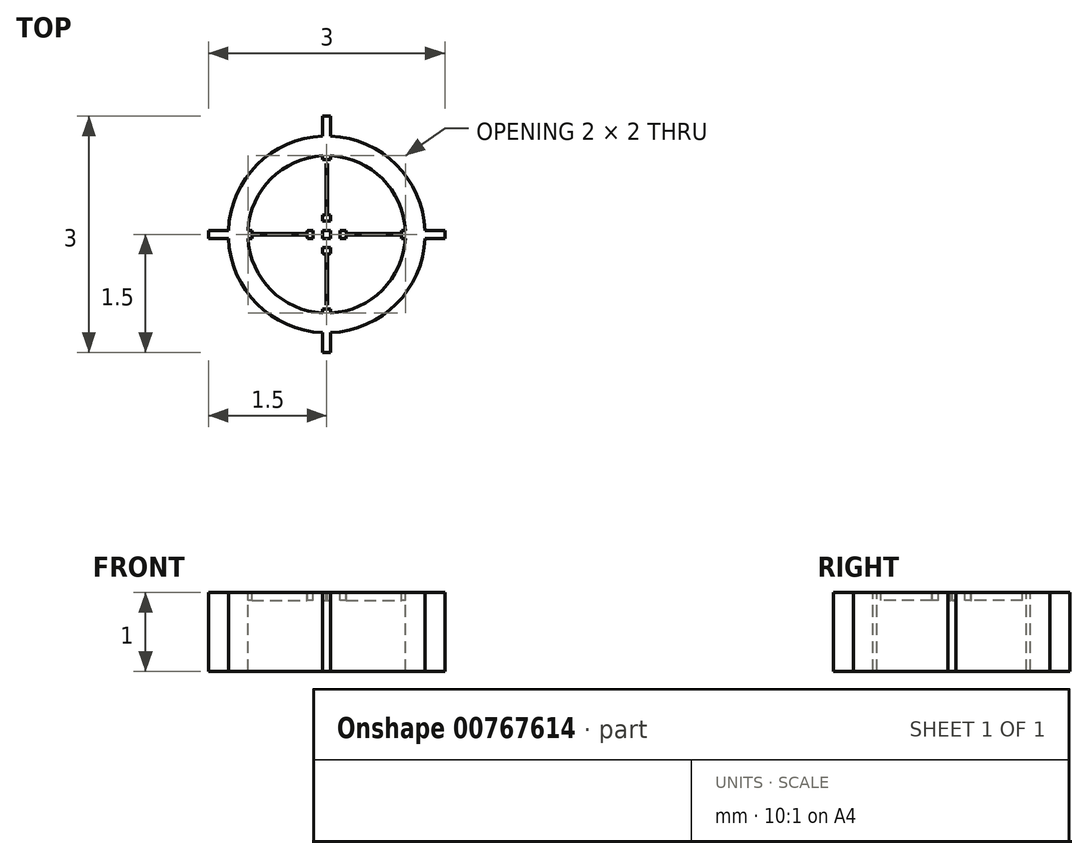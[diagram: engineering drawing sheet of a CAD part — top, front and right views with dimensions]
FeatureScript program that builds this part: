
annotation { "Feature Type Name" : "Feature", "Feature Type Description" : "" }
export const myFeature = defineFeature(function(context is Context, id is Id, definition is map)
    precondition{}
    {
        {
            var Q0;
            Q0=qCreatedBy(makeId("Top.planeOp"),FACE);
            var sketch = newSketch(context, id + "F0", { "sketchPlane" : qUnion([Q0])});
            skCircle(sketch, "E0", {"center": v(0, 0) * mm, "radius": 1 * mm});
            skCircle(sketch, "E1", {"center": v(0, 0) * mm, "radius": 1.25 * mm});
            skLineSegment(sketch, "E2.bottom", {"start": v(1.5, 0.05) * mm, "end": v(-1.5, 0.05) * mm});
            skLineSegment(sketch, "E2.top", {"start": v(1.5, -0.05) * mm, "end": v(-1.5, -0.05) * mm});
            skLineSegment(sketch, "E2.left", {"start": v(1.5, 0.05) * mm, "end": v(1.5, -0.05) * mm});
            skLineSegment(sketch, "E2.right", {"start": v(-1.5, 0.05) * mm, "end": v(-1.5, -0.05) * mm});
            skLineSegment(sketch, "E3.bottom", {"start": v(0.05, 1.5) * mm, "end": v(-0.05, 1.5) * mm});
            skLineSegment(sketch, "E3.top", {"start": v(0.05, -1.5) * mm, "end": v(-0.05, -1.5) * mm});
            skLineSegment(sketch, "E3.left", {"start": v(0.05, 1.5) * mm, "end": v(0.05, -1.5) * mm});
            skLineSegment(sketch, "E3.right", {"start": v(-0.05, 1.5) * mm, "end": v(-0.05, -1.5) * mm});
            skCircle(sketch, "E4", {"center": v(0, 0) * mm, "radius": 0.04 * mm});
            skLineSegment(sketch, "E5.bottom", {"start": v(-0.95, 0.05) * mm, "end": v(-0.17, 0.05) * mm});
            skLineSegment(sketch, "E5.top", {"start": v(-0.95, -0.05) * mm, "end": v(-0.17, -0.05) * mm});
            skLineSegment(sketch, "E5.left", {"start": v(-0.95, 0.05) * mm, "end": v(-0.95, -0.05) * mm});
            skLineSegment(sketch, "E5.right", {"start": v(-0.17, 0.05) * mm, "end": v(-0.17, -0.05) * mm});
            skLineSegment(sketch, "E6.bottom", {"start": v(-0.95, 0) * mm, "end": v(-0.17, 0) * mm});
            skLineSegment(sketch, "E6.top", {"start": v(-0.95, -0.01) * mm, "end": v(-0.17, -0.01) * mm});
            skLineSegment(sketch, "E6.left", {"start": v(-0.95, 0) * mm, "end": v(-0.95, -0.01) * mm});
            skLineSegment(sketch, "E6.right", {"start": v(-0.17, 0) * mm, "end": v(-0.17, -0.01) * mm});
            skLineSegment(sketch, "E7.bottom", {"start": v(0.17, 0.05) * mm, "end": v(0.95, 0.05) * mm});
            skLineSegment(sketch, "E7.top", {"start": v(0.17, -0.05) * mm, "end": v(0.95, -0.05) * mm});
            skLineSegment(sketch, "E7.left", {"start": v(0.17, 0.05) * mm, "end": v(0.17, -0.05) * mm});
            skLineSegment(sketch, "E7.right", {"start": v(0.95, 0.05) * mm, "end": v(0.95, -0.05) * mm});
            skLineSegment(sketch, "E8.bottom", {"start": v(0.17, 0) * mm, "end": v(0.95, 0) * mm});
            skLineSegment(sketch, "E8.top", {"start": v(0.17, -0.01) * mm, "end": v(0.95, -0.01) * mm});
            skLineSegment(sketch, "E8.left", {"start": v(0.17, 0) * mm, "end": v(0.17, -0.01) * mm});
            skLineSegment(sketch, "E8.right", {"start": v(0.95, 0) * mm, "end": v(0.95, -0.01) * mm});
            skLineSegment(sketch, "E9.bottom", {"start": v(-0.05, 0.95) * mm, "end": v(0.05, 0.95) * mm});
            skLineSegment(sketch, "E9.top", {"start": v(-0.05, 0.17) * mm, "end": v(0.05, 0.17) * mm});
            skLineSegment(sketch, "E9.left", {"start": v(-0.05, 0.95) * mm, "end": v(-0.05, 0.17) * mm});
            skLineSegment(sketch, "E9.right", {"start": v(0.05, 0.95) * mm, "end": v(0.05, 0.17) * mm});
            skLineSegment(sketch, "E10.bottom", {"start": v(0, 0.95) * mm, "end": v(0.01, 0.95) * mm});
            skLineSegment(sketch, "E10.top", {"start": v(0, 0.17) * mm, "end": v(0.01, 0.17) * mm});
            skLineSegment(sketch, "E10.left", {"start": v(0, 0.95) * mm, "end": v(0, 0.17) * mm});
            skLineSegment(sketch, "E10.right", {"start": v(0.01, 0.95) * mm, "end": v(0.01, 0.17) * mm});
            skLineSegment(sketch, "E11.bottom", {"start": v(-0.05, -0.95) * mm, "end": v(0.05, -0.95) * mm});
            skLineSegment(sketch, "E11.top", {"start": v(-0.05, -0.17) * mm, "end": v(0.05, -0.17) * mm});
            skLineSegment(sketch, "E11.left", {"start": v(-0.05, -0.95) * mm, "end": v(-0.05, -0.17) * mm});
            skLineSegment(sketch, "E11.right", {"start": v(0.05, -0.95) * mm, "end": v(0.05, -0.17) * mm});
            skLineSegment(sketch, "E12.bottom", {"start": v(0, -0.17) * mm, "end": v(0.01, -0.17) * mm});
            skLineSegment(sketch, "E12.top", {"start": v(0, -0.95) * mm, "end": v(0.01, -0.95) * mm});
            skLineSegment(sketch, "E12.left", {"start": v(0, -0.17) * mm, "end": v(0, -0.95) * mm});
            skLineSegment(sketch, "E12.right", {"start": v(0.01, -0.17) * mm, "end": v(0.01, -0.95) * mm});
            skCircle(sketch, "E13", {"center": v(0, 0) * mm, "radius": 0.9 * mm});
            skCircle(sketch, "E14", {"center": v(0, 0) * mm, "radius": 0.25 * mm});
            skSolve(sketch);
        }
        {
            var Q0;
            Q0=makeQuery(id+"F0.imprint","IMPRINT",FACE,{"disambiguationData":[TD([[makeQuery(id+"F0.imprint","IMPRINT",EDGE,{"derivedFrom":sQuery(id+"F0.wireOp",EDGE,"E0")}),-1.0]])]});
            var Q1;
            {var subQ3=sQuery(id+"F0.wireOp",EDGE,"E6.left");Q1=makeQuery(id+"F0.imprint","IMPRINT",FACE,{"disambiguationData":[TD([[makeQuery(id+"F0.imprint","IMPRINT",EDGE,{"derivedFrom":subQ3}),-1.0]])]});}
            var Q2;
            {var subQ0=sQuery(id+"F0.wireOp",EDGE,"E3.left");var subQ1=sQuery(id+"F0.wireOp",EDGE,"E0");var subQ2=makeQuery(id+"F0.imprint","INTERSECT",VERTEX,{"disambiguationData":[OD(0.0)],"derivedFrom":[subQ1,subQ0]});Q2=makeQuery(id+"F0.imprint","IMPRINT",FACE,{"disambiguationData":[TD([[makeQuery(id+"F0.imprint","IMPRINT",EDGE,{"disambiguationData":[TD([[subQ2,-1.0]])],"derivedFrom":subQ1}),1.0]])]});}
            var Q3;
            {var subQ0=sQuery(id+"F0.wireOp",EDGE,"E3.right");var subQ1=sQuery(id+"F0.wireOp",EDGE,"E0");var subQ2=makeQuery(id+"F0.imprint","INTERSECT",VERTEX,{"disambiguationData":[OD(1.0)],"derivedFrom":[subQ1,subQ0]});Q3=makeQuery(id+"F0.imprint","IMPRINT",FACE,{"disambiguationData":[TD([[makeQuery(id+"F0.imprint","IMPRINT",EDGE,{"disambiguationData":[TD([[subQ2,-1.0]])],"derivedFrom":subQ1}),1.0]])]});}
            var Q4;
            {var subQ7=sQuery(id+"F0.wireOp",EDGE,"E8.right");Q4=makeQuery(id+"F0.imprint","IMPRINT",FACE,{"disambiguationData":[TD([[makeQuery(id+"F0.imprint","IMPRINT",EDGE,{"derivedFrom":subQ7}),1.0]])]});}
            var Q5;
            {var subQ5=sQuery(id+"F0.wireOp",EDGE,"E2.right");Q5=makeQuery(id+"F0.imprint","IMPRINT",FACE,{"disambiguationData":[TD([[makeQuery(id+"F0.imprint","IMPRINT",EDGE,{"derivedFrom":subQ5}),1.0]])]});}
            var Q6;
            {var subQ5=sQuery(id+"F0.wireOp",EDGE,"E3.bottom");Q6=makeQuery(id+"F0.imprint","IMPRINT",FACE,{"disambiguationData":[TD([[makeQuery(id+"F0.imprint","IMPRINT",EDGE,{"derivedFrom":subQ5}),1.0]])]});}
            var Q7;
            {var subQ5=sQuery(id+"F0.wireOp",EDGE,"E2.left");Q7=makeQuery(id+"F0.imprint","IMPRINT",FACE,{"disambiguationData":[TD([[makeQuery(id+"F0.imprint","IMPRINT",EDGE,{"derivedFrom":subQ5}),-1.0]])]});}
            var Q8;
            {var subQ5=sQuery(id+"F0.wireOp",EDGE,"E3.top");Q8=makeQuery(id+"F0.imprint","IMPRINT",FACE,{"disambiguationData":[TD([[makeQuery(id+"F0.imprint","IMPRINT",EDGE,{"derivedFrom":subQ5}),-1.0]])]});}
            extrude(context, id + "F1", {"entities" : qUnion([Q0, Q1, Q2, Q3, Q4, Q5, Q6, Q7, Q8]), "oppositeDirection" : true, "depth" : 1 * mm, "offsetDistance" : 25 * mm});
        }
        {
            var Q0;
            {var subQ5=sQuery(id+"F0.wireOp",EDGE,"E2.right");Q0=makeQuery(id+"F0.imprint","IMPRINT",FACE,{"disambiguationData":[TD([[makeQuery(id+"F0.imprint","IMPRINT",EDGE,{"derivedFrom":subQ5}),1.0]])]});}
            var Q1;
            {var subQ0=sQuery(id+"F0.wireOp",EDGE,"E2.bottom");var subQ1=sQuery(id+"F0.wireOp",EDGE,"E0");var subQ2=makeQuery(id+"F0.imprint","INTERSECT",VERTEX,{"disambiguationData":[OD(1.0)],"derivedFrom":[subQ1,subQ0]});Q1=makeQuery(id+"F0.imprint","IMPRINT",FACE,{"disambiguationData":[TD([[makeQuery(id+"F0.imprint","IMPRINT",EDGE,{"disambiguationData":[TD([[subQ2,-1.0]])],"derivedFrom":subQ1}),-1.0]])]});}
            var Q2;
            {var subQ0=sQuery(id+"F0.wireOp",EDGE,"E2.bottom");var subQ1=sQuery(id+"F0.wireOp",EDGE,"E0");var subQ2=makeQuery(id+"F0.imprint","INTERSECT",VERTEX,{"disambiguationData":[OD(1.0)],"derivedFrom":[subQ1,subQ0]});Q2=makeQuery(id+"F0.imprint","IMPRINT",FACE,{"disambiguationData":[TD([[makeQuery(id+"F0.imprint","IMPRINT",EDGE,{"disambiguationData":[TD([[subQ2,-1.0]])],"derivedFrom":subQ1}),1.0]])]});}
            var Q3;
            {var subQ0=sQuery(id+"F0.wireOp",EDGE,"E2.bottom");var subQ1=sQuery(id+"F0.wireOp",EDGE,"E0");var subQ2=makeQuery(id+"F0.imprint","INTERSECT",VERTEX,{"disambiguationData":[OD(0.0)],"derivedFrom":[subQ1,subQ0]});Q3=makeQuery(id+"F0.imprint","IMPRINT",FACE,{"disambiguationData":[TD([[makeQuery(id+"F0.imprint","IMPRINT",EDGE,{"disambiguationData":[TD([[subQ2,1.0]])],"derivedFrom":subQ1}),1.0]])]});}
            var Q4;
            {var subQ0=sQuery(id+"F0.wireOp",EDGE,"E2.bottom");var subQ1=sQuery(id+"F0.wireOp",EDGE,"E0");var subQ2=makeQuery(id+"F0.imprint","INTERSECT",VERTEX,{"disambiguationData":[OD(0.0)],"derivedFrom":[subQ1,subQ0]});Q4=makeQuery(id+"F0.imprint","IMPRINT",FACE,{"disambiguationData":[TD([[makeQuery(id+"F0.imprint","IMPRINT",EDGE,{"disambiguationData":[TD([[subQ2,1.0]])],"derivedFrom":subQ1}),-1.0]])]});}
            var Q5;
            {var subQ5=sQuery(id+"F0.wireOp",EDGE,"E2.left");Q5=makeQuery(id+"F0.imprint","IMPRINT",FACE,{"disambiguationData":[TD([[makeQuery(id+"F0.imprint","IMPRINT",EDGE,{"derivedFrom":subQ5}),-1.0]])]});}
            var Q6;
            {var subQ0=sQuery(id+"F0.wireOp",EDGE,"E3.left");var subQ1=sQuery(id+"F0.wireOp",EDGE,"E0");var subQ2=makeQuery(id+"F0.imprint","INTERSECT",VERTEX,{"disambiguationData":[OD(0.0)],"derivedFrom":[subQ1,subQ0]});Q6=makeQuery(id+"F0.imprint","IMPRINT",FACE,{"disambiguationData":[TD([[makeQuery(id+"F0.imprint","IMPRINT",EDGE,{"disambiguationData":[TD([[subQ2,-1.0]])],"derivedFrom":subQ1}),1.0]])]});}
            var Q7;
            {var subQ0=sQuery(id+"F0.wireOp",EDGE,"E3.left");var subQ1=sQuery(id+"F0.wireOp",EDGE,"E0");var subQ2=makeQuery(id+"F0.imprint","INTERSECT",VERTEX,{"disambiguationData":[OD(0.0)],"derivedFrom":[subQ1,subQ0]});Q7=makeQuery(id+"F0.imprint","IMPRINT",FACE,{"disambiguationData":[TD([[makeQuery(id+"F0.imprint","IMPRINT",EDGE,{"disambiguationData":[TD([[subQ2,-1.0]])],"derivedFrom":subQ1}),-1.0]])]});}
            var Q8;
            {var subQ5=sQuery(id+"F0.wireOp",EDGE,"E3.bottom");Q8=makeQuery(id+"F0.imprint","IMPRINT",FACE,{"disambiguationData":[TD([[makeQuery(id+"F0.imprint","IMPRINT",EDGE,{"derivedFrom":subQ5}),1.0]])]});}
            var Q9;
            {var subQ0=sQuery(id+"F0.wireOp",EDGE,"E3.right");var subQ1=sQuery(id+"F0.wireOp",EDGE,"E0");var subQ2=makeQuery(id+"F0.imprint","INTERSECT",VERTEX,{"disambiguationData":[OD(1.0)],"derivedFrom":[subQ1,subQ0]});Q9=makeQuery(id+"F0.imprint","IMPRINT",FACE,{"disambiguationData":[TD([[makeQuery(id+"F0.imprint","IMPRINT",EDGE,{"disambiguationData":[TD([[subQ2,-1.0]])],"derivedFrom":subQ1}),1.0]])]});}
            var Q10;
            {var subQ0=sQuery(id+"F0.wireOp",EDGE,"E3.right");var subQ1=sQuery(id+"F0.wireOp",EDGE,"E0");var subQ2=makeQuery(id+"F0.imprint","INTERSECT",VERTEX,{"disambiguationData":[OD(1.0)],"derivedFrom":[subQ1,subQ0]});Q10=makeQuery(id+"F0.imprint","IMPRINT",FACE,{"disambiguationData":[TD([[makeQuery(id+"F0.imprint","IMPRINT",EDGE,{"disambiguationData":[TD([[subQ2,-1.0]])],"derivedFrom":subQ1}),-1.0]])]});}
            var Q11;
            {var subQ5=sQuery(id+"F0.wireOp",EDGE,"E3.top");Q11=makeQuery(id+"F0.imprint","IMPRINT",FACE,{"disambiguationData":[TD([[makeQuery(id+"F0.imprint","IMPRINT",EDGE,{"derivedFrom":subQ5}),-1.0]])]});}
            var Q12;
            Q12=makeQuery(id+"F0.imprint","IMPRINT",FACE,{"disambiguationData":[TD([[makeQuery(id+"F0.imprint","IMPRINT",EDGE,{"derivedFrom":sQuery(id+"F0.wireOp",EDGE,"E4")}),1.0]])]});
            var Q13;
            Q13=makeQuery(id+"F0.imprint","IMPRINT",FACE,{"disambiguationData":[TD([[makeQuery(id+"F0.imprint","IMPRINT",EDGE,{"derivedFrom":sQuery(id+"F0.wireOp",EDGE,"E4")}),-1.0]])]});
            var Q14;
            Q14=makeQuery(id+"F0.imprint","IMPRINT",FACE,{"disambiguationData":[TD([[makeQuery(id+"F0.imprint","IMPRINT",EDGE,{"derivedFrom":sQuery(id+"F0.wireOp",EDGE,"E6.bottom")}),-1.0]])]});
            var Q15;
            {var subQ7=sQuery(id+"F0.wireOp",EDGE,"E6.right");Q15=makeQuery(id+"F0.imprint","IMPRINT",FACE,{"disambiguationData":[TD([[makeQuery(id+"F0.imprint","IMPRINT",EDGE,{"derivedFrom":subQ7}),1.0]])]});}
            var Q16;
            {var subQ5=sQuery(id+"F0.wireOp",EDGE,"E8.left");Q16=makeQuery(id+"F0.imprint","IMPRINT",FACE,{"disambiguationData":[TD([[makeQuery(id+"F0.imprint","IMPRINT",EDGE,{"derivedFrom":subQ5}),-1.0]])]});}
            var Q17;
            {var subQ8=sQuery(id+"F0.wireOp",EDGE,"E12.bottom");Q17=makeQuery(id+"F0.imprint","IMPRINT",FACE,{"disambiguationData":[TD([[makeQuery(id+"F0.imprint","IMPRINT",EDGE,{"derivedFrom":subQ8}),1.0]])]});}
            var Q18;
            Q18=makeQuery(id+"F0.imprint","IMPRINT",FACE,{"disambiguationData":[TD([[makeQuery(id+"F0.imprint","IMPRINT",EDGE,{"derivedFrom":sQuery(id+"F0.wireOp",EDGE,"E10.bottom")}),-1.0]])]});
            var Q19;
            Q19=makeQuery(id+"F0.imprint","IMPRINT",FACE,{"disambiguationData":[TD([[makeQuery(id+"F0.imprint","IMPRINT",EDGE,{"derivedFrom":sQuery(id+"F0.wireOp",EDGE,"E12.bottom")}),-1.0]])]});
            var Q20;
            Q20=makeQuery(id+"F0.imprint","IMPRINT",FACE,{"disambiguationData":[TD([[makeQuery(id+"F0.imprint","IMPRINT",EDGE,{"derivedFrom":sQuery(id+"F0.wireOp",EDGE,"E8.bottom")}),-1.0]])]});
            var Q21;
            {var subQ3=sQuery(id+"F0.wireOp",EDGE,"E10.top");Q21=makeQuery(id+"F0.imprint","IMPRINT",FACE,{"disambiguationData":[TD([[makeQuery(id+"F0.imprint","IMPRINT",EDGE,{"derivedFrom":subQ3}),-1.0]])]});}
            var Q22;
            {var subQ0=sQuery(id+"F0.wireOp",EDGE,"E10.top");Q22=makeQuery(id+"F0.imprint","IMPRINT",FACE,{"disambiguationData":[TD([[makeQuery(id+"F0.imprint","IMPRINT",EDGE,{"derivedFrom":subQ0}),1.0]])]});}
            var Q23;
            {var subQ0=sQuery(id+"F0.wireOp",EDGE,"E12.top");Q23=makeQuery(id+"F0.imprint","IMPRINT",FACE,{"disambiguationData":[TD([[makeQuery(id+"F0.imprint","IMPRINT",EDGE,{"derivedFrom":subQ0}),1.0]])]});}
            var Q24;
            {var subQ0=sQuery(id+"F0.wireOp",EDGE,"E9.left");var subQ5=sQuery(id+"F0.wireOp",EDGE,"E14");var subQ6=makeQuery(id+"F0.imprint","INTERSECT",VERTEX,{"derivedFrom":[subQ0,subQ5]});Q24=makeQuery(id+"F0.imprint","IMPRINT",FACE,{"disambiguationData":[TD([[makeQuery(id+"F0.imprint","IMPRINT",EDGE,{"disambiguationData":[TD([[subQ6,1.0]])],"derivedFrom":subQ5}),1.0]])]});}
            var Q25;
            {var subQ0=sQuery(id+"F0.wireOp",EDGE,"E9.right");var subQ5=sQuery(id+"F0.wireOp",EDGE,"E14");var subQ6=makeQuery(id+"F0.imprint","INTERSECT",VERTEX,{"derivedFrom":[subQ0,subQ5]});Q25=makeQuery(id+"F0.imprint","IMPRINT",FACE,{"disambiguationData":[TD([[makeQuery(id+"F0.imprint","IMPRINT",EDGE,{"disambiguationData":[TD([[subQ6,-1.0]])],"derivedFrom":subQ5}),1.0]])]});}
            var Q26;
            {var subQ1=sQuery(id+"F0.wireOp",EDGE,"E7.bottom");var subQ3=sQuery(id+"F0.wireOp",EDGE,"E14");var subQ4=makeQuery(id+"F0.imprint","INTERSECT",VERTEX,{"derivedFrom":[subQ1,subQ3]});Q26=makeQuery(id+"F0.imprint","IMPRINT",FACE,{"disambiguationData":[TD([[makeQuery(id+"F0.imprint","IMPRINT",EDGE,{"disambiguationData":[TD([[subQ4,1.0]])],"derivedFrom":subQ3}),1.0]])]});}
            var Q27;
            {var subQ1=sQuery(id+"F0.wireOp",EDGE,"E7.top");var subQ3=sQuery(id+"F0.wireOp",EDGE,"E14");var subQ4=makeQuery(id+"F0.imprint","INTERSECT",VERTEX,{"derivedFrom":[subQ1,subQ3]});Q27=makeQuery(id+"F0.imprint","IMPRINT",FACE,{"disambiguationData":[TD([[makeQuery(id+"F0.imprint","IMPRINT",EDGE,{"disambiguationData":[TD([[subQ4,-1.0]])],"derivedFrom":subQ3}),1.0]])]});}
            var Q28;
            {var subQ3=sQuery(id+"F0.wireOp",EDGE,"E14");var subQ7=sQuery(id+"F0.wireOp",EDGE,"E7.top");var subQ9=makeQuery(id+"F0.imprint","INTERSECT",VERTEX,{"derivedFrom":[subQ7,subQ3]});Q28=makeQuery(id+"F0.imprint","IMPRINT",FACE,{"disambiguationData":[TD([[makeQuery(id+"F0.imprint","IMPRINT",EDGE,{"disambiguationData":[TD([[subQ9,1.0]])],"derivedFrom":subQ3}),1.0]])]});}
            var Q29;
            {var subQ0=sQuery(id+"F0.wireOp",EDGE,"E11.right");var subQ5=sQuery(id+"F0.wireOp",EDGE,"E14");var subQ6=makeQuery(id+"F0.imprint","INTERSECT",VERTEX,{"derivedFrom":[subQ0,subQ5]});Q29=makeQuery(id+"F0.imprint","IMPRINT",FACE,{"disambiguationData":[TD([[makeQuery(id+"F0.imprint","IMPRINT",EDGE,{"disambiguationData":[TD([[subQ6,1.0]])],"derivedFrom":subQ5}),1.0]])]});}
            var Q30;
            {var subQ0=sQuery(id+"F0.wireOp",EDGE,"E11.left");var subQ5=sQuery(id+"F0.wireOp",EDGE,"E14");var subQ7=makeQuery(id+"F0.imprint","INTERSECT",VERTEX,{"derivedFrom":[subQ0,subQ5]});Q30=makeQuery(id+"F0.imprint","IMPRINT",FACE,{"disambiguationData":[TD([[makeQuery(id+"F0.imprint","IMPRINT",EDGE,{"disambiguationData":[TD([[subQ7,-1.0]])],"derivedFrom":subQ5}),1.0]])]});}
            var Q31;
            {var subQ3=sQuery(id+"F0.wireOp",EDGE,"E14");var subQ5=sQuery(id+"F0.wireOp",EDGE,"E5.top");var subQ8=makeQuery(id+"F0.imprint","INTERSECT",VERTEX,{"derivedFrom":[subQ5,subQ3]});Q31=makeQuery(id+"F0.imprint","IMPRINT",FACE,{"disambiguationData":[TD([[makeQuery(id+"F0.imprint","IMPRINT",EDGE,{"disambiguationData":[TD([[subQ8,-1.0]])],"derivedFrom":subQ3}),1.0]])]});}
            var Q32;
            {var subQ1=sQuery(id+"F0.wireOp",EDGE,"E5.top");var subQ3=sQuery(id+"F0.wireOp",EDGE,"E14");var subQ4=makeQuery(id+"F0.imprint","INTERSECT",VERTEX,{"derivedFrom":[subQ1,subQ3]});Q32=makeQuery(id+"F0.imprint","IMPRINT",FACE,{"disambiguationData":[TD([[makeQuery(id+"F0.imprint","IMPRINT",EDGE,{"disambiguationData":[TD([[subQ4,1.0]])],"derivedFrom":subQ3}),1.0]])]});}
            var Q33;
            {var subQ1=sQuery(id+"F0.wireOp",EDGE,"E5.bottom");var subQ3=sQuery(id+"F0.wireOp",EDGE,"E14");var subQ4=makeQuery(id+"F0.imprint","INTERSECT",VERTEX,{"derivedFrom":[subQ1,subQ3]});Q33=makeQuery(id+"F0.imprint","IMPRINT",FACE,{"disambiguationData":[TD([[makeQuery(id+"F0.imprint","IMPRINT",EDGE,{"disambiguationData":[TD([[subQ4,-1.0]])],"derivedFrom":subQ3}),1.0]])]});}
            var Q34;
            {var subQ3=sQuery(id+"F0.wireOp",EDGE,"E14");var subQ5=sQuery(id+"F0.wireOp",EDGE,"E5.bottom");var subQ8=makeQuery(id+"F0.imprint","INTERSECT",VERTEX,{"derivedFrom":[subQ5,subQ3]});Q34=makeQuery(id+"F0.imprint","IMPRINT",FACE,{"disambiguationData":[TD([[makeQuery(id+"F0.imprint","IMPRINT",EDGE,{"disambiguationData":[TD([[subQ8,1.0]])],"derivedFrom":subQ3}),1.0]])]});}
            var Q35;
            {var subQ3=sQuery(id+"F0.wireOp",EDGE,"E14");var subQ5=sQuery(id+"F0.wireOp",EDGE,"E7.bottom");var subQ6=makeQuery(id+"F0.imprint","INTERSECT",VERTEX,{"derivedFrom":[subQ5,subQ3]});Q35=makeQuery(id+"F0.imprint","IMPRINT",FACE,{"disambiguationData":[TD([[makeQuery(id+"F0.imprint","IMPRINT",EDGE,{"disambiguationData":[TD([[subQ6,-1.0]])],"derivedFrom":subQ3}),1.0]])]});}
            var Q36;
            {var subQ0=sQuery(id+"F0.wireOp",EDGE,"E13");var subQ1=sQuery(id+"F0.wireOp",EDGE,"E10.left");var subQ2=makeQuery(id+"F0.imprint","INTERSECT",VERTEX,{"derivedFrom":[subQ1,subQ0]});Q36=makeQuery(id+"F0.imprint","IMPRINT",FACE,{"disambiguationData":[TD([[makeQuery(id+"F0.imprint","IMPRINT",EDGE,{"disambiguationData":[TD([[subQ2,-1.0]])],"derivedFrom":subQ1}),1.0]])]});}
            var Q37;
            {var subQ0=sQuery(id+"F0.wireOp",EDGE,"E14");var subQ1=sQuery(id+"F0.wireOp",EDGE,"E12.left");var subQ2=makeQuery(id+"F0.imprint","INTERSECT",VERTEX,{"derivedFrom":[subQ1,subQ0]});Q37=makeQuery(id+"F0.imprint","IMPRINT",FACE,{"disambiguationData":[TD([[makeQuery(id+"F0.imprint","IMPRINT",EDGE,{"disambiguationData":[TD([[subQ2,-1.0]])],"derivedFrom":subQ1}),1.0]])]});}
            extrude(context, id + "F2", {"entities" : qUnion([Q0, Q1, Q2, Q3, Q4, Q5, Q6, Q7, Q8, Q9, Q10, Q11, Q12, Q13, Q14, Q15, Q16, Q17, Q18, Q19, Q20, Q21, Q22, Q23, Q24, Q25, Q26, Q27, Q28, Q29, Q30, Q31, Q32, Q33, Q34, Q35, Q36, Q37]), "operationType" : NewBodyOperationType.ADD, "oppositeDirection" : true, "depth" : 0.1 * mm, "offsetDistance" : 25 * mm});
        }
        {
            var Q0;
            {var subQ0=sQuery(id+"F0.wireOp",EDGE,"E13");var subQ1=sQuery(id+"F0.wireOp",EDGE,"E6.bottom");var subQ2=makeQuery(id+"F0.imprint","INTERSECT",VERTEX,{"derivedFrom":[subQ1,subQ0]});Q0=makeQuery(id+"F0.imprint","IMPRINT",FACE,{"disambiguationData":[TD([[makeQuery(id+"F0.imprint","IMPRINT",EDGE,{"disambiguationData":[TD([[subQ2,-1.0]])],"derivedFrom":subQ1}),-1.0]])]});}
            var Q1;
            {var subQ0=sQuery(id+"F0.wireOp",EDGE,"E13");var subQ1=sQuery(id+"F0.wireOp",EDGE,"E5.bottom");var subQ2=makeQuery(id+"F0.imprint","INTERSECT",VERTEX,{"derivedFrom":[subQ1,subQ0]});Q1=makeQuery(id+"F0.imprint","IMPRINT",FACE,{"disambiguationData":[TD([[makeQuery(id+"F0.imprint","IMPRINT",EDGE,{"disambiguationData":[TD([[subQ2,-1.0]])],"derivedFrom":subQ1}),-1.0]])]});}
            var Q2;
            {var subQ0=sQuery(id+"F0.wireOp",EDGE,"E13");var subQ1=sQuery(id+"F0.wireOp",EDGE,"E5.bottom");var subQ2=makeQuery(id+"F0.imprint","INTERSECT",VERTEX,{"derivedFrom":[subQ1,subQ0]});Q2=makeQuery(id+"F0.imprint","IMPRINT",FACE,{"disambiguationData":[TD([[makeQuery(id+"F0.imprint","IMPRINT",EDGE,{"disambiguationData":[TD([[subQ2,-1.0]])],"derivedFrom":subQ1}),1.0]])]});}
            var Q3;
            {var subQ0=sQuery(id+"F0.wireOp",EDGE,"E13");var subQ1=sQuery(id+"F0.wireOp",EDGE,"E9.left");var subQ2=makeQuery(id+"F0.imprint","INTERSECT",VERTEX,{"derivedFrom":[subQ1,subQ0]});Q3=makeQuery(id+"F0.imprint","IMPRINT",FACE,{"disambiguationData":[TD([[makeQuery(id+"F0.imprint","IMPRINT",EDGE,{"disambiguationData":[TD([[subQ2,-1.0]])],"derivedFrom":subQ1}),1.0]])]});}
            var Q4;
            {var subQ0=sQuery(id+"F0.wireOp",EDGE,"E13");var subQ1=sQuery(id+"F0.wireOp",EDGE,"E10.left");var subQ2=makeQuery(id+"F0.imprint","INTERSECT",VERTEX,{"derivedFrom":[subQ1,subQ0]});Q4=makeQuery(id+"F0.imprint","IMPRINT",FACE,{"disambiguationData":[TD([[makeQuery(id+"F0.imprint","IMPRINT",EDGE,{"disambiguationData":[TD([[subQ2,-1.0]])],"derivedFrom":subQ1}),1.0]])]});}
            var Q5;
            {var subQ0=sQuery(id+"F0.wireOp",EDGE,"E13");var subQ1=sQuery(id+"F0.wireOp",EDGE,"E9.right");var subQ2=makeQuery(id+"F0.imprint","INTERSECT",VERTEX,{"derivedFrom":[subQ1,subQ0]});Q5=makeQuery(id+"F0.imprint","IMPRINT",FACE,{"disambiguationData":[TD([[makeQuery(id+"F0.imprint","IMPRINT",EDGE,{"disambiguationData":[TD([[subQ2,-1.0]])],"derivedFrom":subQ1}),-1.0]])]});}
            var Q6;
            {var subQ0=sQuery(id+"F0.wireOp",EDGE,"E14");var subQ1=sQuery(id+"F0.wireOp",EDGE,"E7.bottom");var subQ2=makeQuery(id+"F0.imprint","INTERSECT",VERTEX,{"derivedFrom":[subQ1,subQ0]});Q6=makeQuery(id+"F0.imprint","IMPRINT",FACE,{"disambiguationData":[TD([[makeQuery(id+"F0.imprint","IMPRINT",EDGE,{"disambiguationData":[TD([[subQ2,-1.0]])],"derivedFrom":subQ1}),1.0]])]});}
            var Q7;
            {var subQ0=sQuery(id+"F0.wireOp",EDGE,"E14");var subQ1=sQuery(id+"F0.wireOp",EDGE,"E7.bottom");var subQ2=makeQuery(id+"F0.imprint","INTERSECT",VERTEX,{"derivedFrom":[subQ1,subQ0]});Q7=makeQuery(id+"F0.imprint","IMPRINT",FACE,{"disambiguationData":[TD([[makeQuery(id+"F0.imprint","IMPRINT",EDGE,{"disambiguationData":[TD([[subQ2,-1.0]])],"derivedFrom":subQ1}),-1.0]])]});}
            var Q8;
            {var subQ0=sQuery(id+"F0.wireOp",EDGE,"E14");var subQ1=sQuery(id+"F0.wireOp",EDGE,"E8.bottom");var subQ2=makeQuery(id+"F0.imprint","INTERSECT",VERTEX,{"derivedFrom":[subQ1,subQ0]});Q8=makeQuery(id+"F0.imprint","IMPRINT",FACE,{"disambiguationData":[TD([[makeQuery(id+"F0.imprint","IMPRINT",EDGE,{"disambiguationData":[TD([[subQ2,-1.0]])],"derivedFrom":subQ1}),-1.0]])]});}
            var Q9;
            {var subQ0=sQuery(id+"F0.wireOp",EDGE,"E14");var subQ1=sQuery(id+"F0.wireOp",EDGE,"E7.top");var subQ2=makeQuery(id+"F0.imprint","INTERSECT",VERTEX,{"derivedFrom":[subQ1,subQ0]});Q9=makeQuery(id+"F0.imprint","IMPRINT",FACE,{"disambiguationData":[TD([[makeQuery(id+"F0.imprint","IMPRINT",EDGE,{"disambiguationData":[TD([[subQ2,-1.0]])],"derivedFrom":subQ1}),1.0]])]});}
            var Q10;
            {var subQ0=sQuery(id+"F0.wireOp",EDGE,"E14");var subQ1=sQuery(id+"F0.wireOp",EDGE,"E7.top");var subQ2=makeQuery(id+"F0.imprint","INTERSECT",VERTEX,{"derivedFrom":[subQ1,subQ0]});Q10=makeQuery(id+"F0.imprint","IMPRINT",FACE,{"disambiguationData":[TD([[makeQuery(id+"F0.imprint","IMPRINT",EDGE,{"disambiguationData":[TD([[subQ2,-1.0]])],"derivedFrom":subQ1}),-1.0]])]});}
            var Q11;
            {var subQ0=sQuery(id+"F0.wireOp",EDGE,"E13");var subQ1=sQuery(id+"F0.wireOp",EDGE,"E11.right");var subQ2=makeQuery(id+"F0.imprint","INTERSECT",VERTEX,{"derivedFrom":[subQ1,subQ0]});Q11=makeQuery(id+"F0.imprint","IMPRINT",FACE,{"disambiguationData":[TD([[makeQuery(id+"F0.imprint","IMPRINT",EDGE,{"disambiguationData":[TD([[subQ2,-1.0]])],"derivedFrom":subQ1}),1.0]])]});}
            var Q12;
            {var subQ0=sQuery(id+"F0.wireOp",EDGE,"E14");var subQ1=sQuery(id+"F0.wireOp",EDGE,"E12.left");var subQ2=makeQuery(id+"F0.imprint","INTERSECT",VERTEX,{"derivedFrom":[subQ1,subQ0]});Q12=makeQuery(id+"F0.imprint","IMPRINT",FACE,{"disambiguationData":[TD([[makeQuery(id+"F0.imprint","IMPRINT",EDGE,{"disambiguationData":[TD([[subQ2,-1.0]])],"derivedFrom":subQ1}),1.0]])]});}
            var Q13;
            {var subQ0=sQuery(id+"F0.wireOp",EDGE,"E13");var subQ1=sQuery(id+"F0.wireOp",EDGE,"E11.left");var subQ2=makeQuery(id+"F0.imprint","INTERSECT",VERTEX,{"derivedFrom":[subQ1,subQ0]});Q13=makeQuery(id+"F0.imprint","IMPRINT",FACE,{"disambiguationData":[TD([[makeQuery(id+"F0.imprint","IMPRINT",EDGE,{"disambiguationData":[TD([[subQ2,-1.0]])],"derivedFrom":subQ1}),-1.0]])]});}
            var Q14;
            {var subQ0=sQuery(id+"F0.wireOp",EDGE,"E13");var subQ1=sQuery(id+"F0.wireOp",EDGE,"E5.top");var subQ2=makeQuery(id+"F0.imprint","INTERSECT",VERTEX,{"derivedFrom":[subQ1,subQ0]});Q14=makeQuery(id+"F0.imprint","IMPRINT",FACE,{"disambiguationData":[TD([[makeQuery(id+"F0.imprint","IMPRINT",EDGE,{"disambiguationData":[TD([[subQ2,-1.0]])],"derivedFrom":subQ1}),-1.0]])]});}
            var Q15;
            {var subQ3=sQuery(id+"F0.wireOp",EDGE,"E14");var subQ5=sQuery(id+"F0.wireOp",EDGE,"E5.bottom");var subQ8=makeQuery(id+"F0.imprint","INTERSECT",VERTEX,{"derivedFrom":[subQ5,subQ3]});Q15=makeQuery(id+"F0.imprint","IMPRINT",FACE,{"disambiguationData":[TD([[makeQuery(id+"F0.imprint","IMPRINT",EDGE,{"disambiguationData":[TD([[subQ8,1.0]])],"derivedFrom":subQ3}),1.0]])]});}
            var Q16;
            {var subQ3=sQuery(id+"F0.wireOp",EDGE,"E14");var subQ5=sQuery(id+"F0.wireOp",EDGE,"E7.bottom");var subQ6=makeQuery(id+"F0.imprint","INTERSECT",VERTEX,{"derivedFrom":[subQ5,subQ3]});Q16=makeQuery(id+"F0.imprint","IMPRINT",FACE,{"disambiguationData":[TD([[makeQuery(id+"F0.imprint","IMPRINT",EDGE,{"disambiguationData":[TD([[subQ6,-1.0]])],"derivedFrom":subQ3}),1.0]])]});}
            var Q17;
            {var subQ3=sQuery(id+"F0.wireOp",EDGE,"E14");var subQ5=sQuery(id+"F0.wireOp",EDGE,"E5.top");var subQ8=makeQuery(id+"F0.imprint","INTERSECT",VERTEX,{"derivedFrom":[subQ5,subQ3]});Q17=makeQuery(id+"F0.imprint","IMPRINT",FACE,{"disambiguationData":[TD([[makeQuery(id+"F0.imprint","IMPRINT",EDGE,{"disambiguationData":[TD([[subQ8,-1.0]])],"derivedFrom":subQ3}),1.0]])]});}
            var Q18;
            {var subQ3=sQuery(id+"F0.wireOp",EDGE,"E14");var subQ7=sQuery(id+"F0.wireOp",EDGE,"E7.top");var subQ9=makeQuery(id+"F0.imprint","INTERSECT",VERTEX,{"derivedFrom":[subQ7,subQ3]});Q18=makeQuery(id+"F0.imprint","IMPRINT",FACE,{"disambiguationData":[TD([[makeQuery(id+"F0.imprint","IMPRINT",EDGE,{"disambiguationData":[TD([[subQ9,1.0]])],"derivedFrom":subQ3}),1.0]])]});}
            extrude(context, id + "F3", {"entities" : qUnion([Q0, Q1, Q2, Q3, Q4, Q5, Q6, Q7, Q8, Q9, Q10, Q11, Q12, Q13, Q14, Q15, Q16, Q17, Q18]), "operationType" : NewBodyOperationType.REMOVE, "oppositeDirection" : true, "depth" : 1 * mm, "offsetDistance" : 25 * mm, "hasSecondDirection" : true, "secondDirectionOppositeDirection" : false, "secondDirectionDepth" : -.2 * mm});
        }
    });
